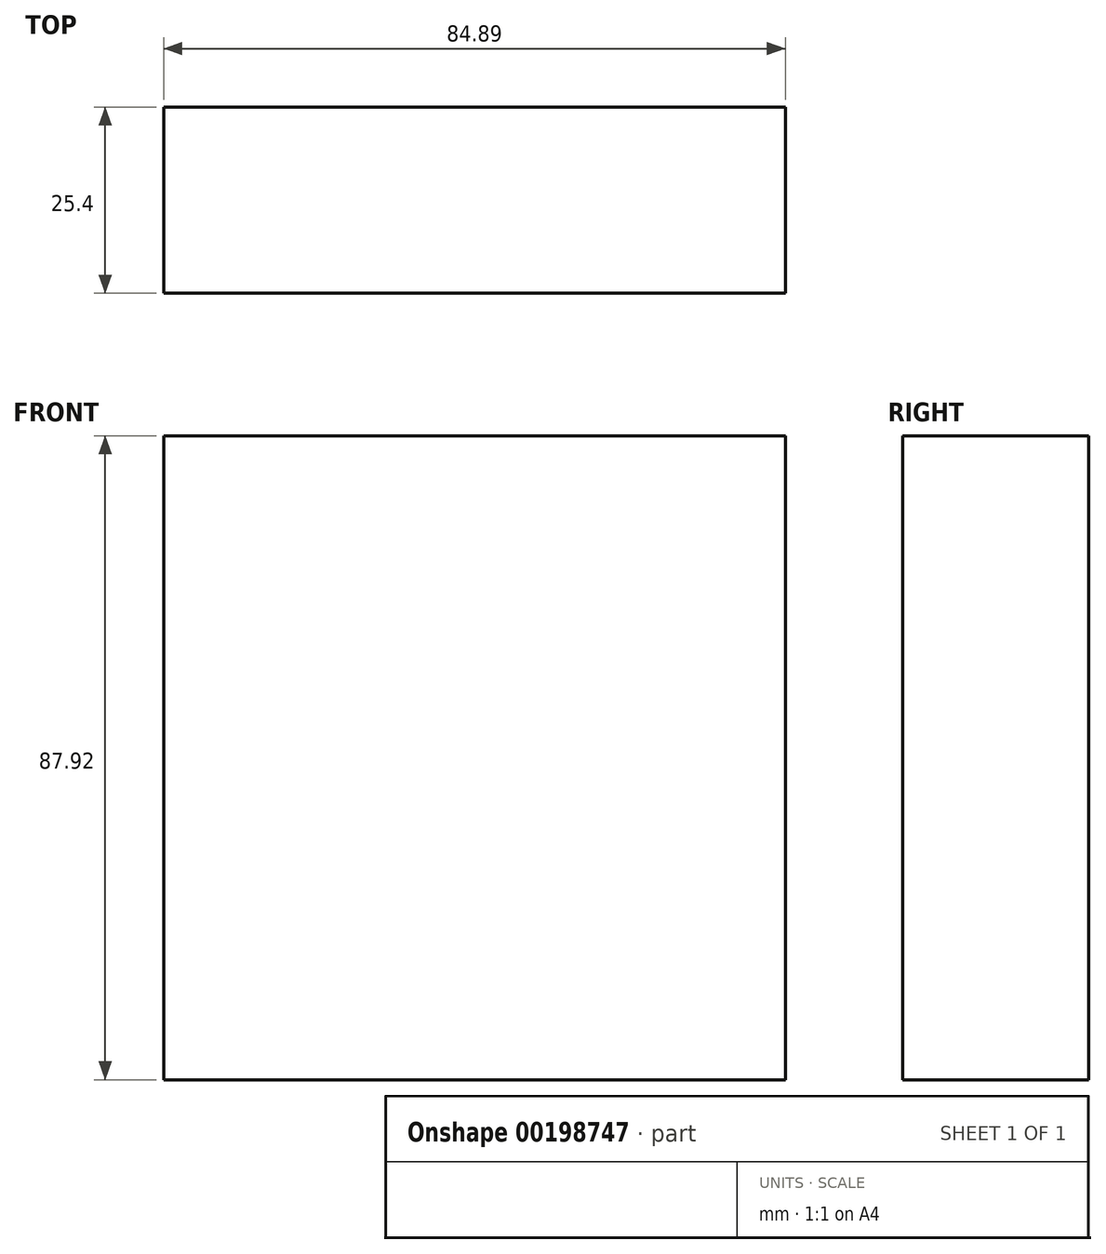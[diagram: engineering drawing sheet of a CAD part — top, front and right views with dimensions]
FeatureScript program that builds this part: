
annotation { "Feature Type Name" : "Feature", "Feature Type Description" : "" }
export const myFeature = defineFeature(function(context is Context, id is Id, definition is map)
    precondition{}
    {
        {
            var Q0;
            Q0=qCreatedBy(makeId("Front.planeOp"),FACE);
            var sketch = newSketch(context, id + "F0", { "sketchPlane" : qUnion([Q0])});
            skLineSegment(sketch, "E0.bottom", {"start": v(-43.26, 43.73) * mm, "end": v(41.63, 43.73) * mm});
            skLineSegment(sketch, "E0.top", {"start": v(-43.26, -44.2) * mm, "end": v(41.63, -44.2) * mm});
            skLineSegment(sketch, "E0.left", {"start": v(-43.26, 43.73) * mm, "end": v(-43.26, -44.2) * mm});
            skLineSegment(sketch, "E0.right", {"start": v(41.63, 43.73) * mm, "end": v(41.63, -44.2) * mm});
            skSolve(sketch);
        }
        {
            var Q0;
            Q0=makeQuery(id+"F0.imprint","IMPRINT",FACE,{"disambiguationData":[TD([[makeQuery(id+"F0.imprint","IMPRINT",EDGE,{"derivedFrom":sQuery(id+"F0.wireOp",EDGE,"E0.bottom")}),-1.0]])]});
            extrude(context, id + "F1", {"entities" : qUnion([Q0]), "oppositeDirection" : true, "depth" : 25.4 * mm});
        }
    });
